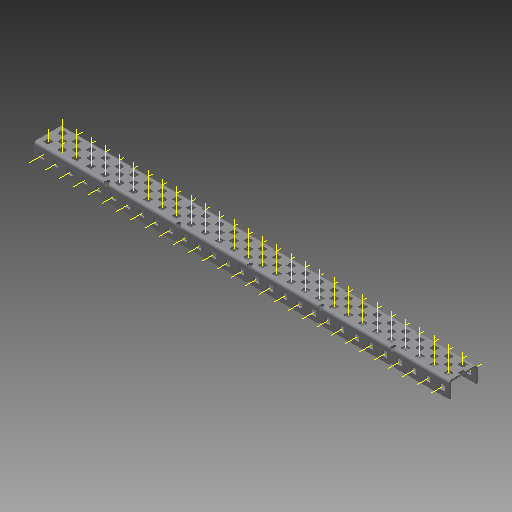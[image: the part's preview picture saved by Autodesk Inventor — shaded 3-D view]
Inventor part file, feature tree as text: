
AUTODESK INVENTOR PART (.ipt)
format: ipt  version: 2017 (Build 210142000, 142)  size: 2,218,496 bytes
history: native  units: in
note: dims shown in document units (in); Inventor stores cm internally (conversion verified against a paired STEP export)
features: other x151, pattern_linear x3, sheet_metal_op x1, extrude x1, imported_body x1, sketch x1
ambient origin geometry x8: Origin, YZ Plane, XZ Plane, XY Plane, X Axis, Y Axis, Z Axis, Center Point
bodies: Body1 (feature_tree)
feature tree (158):
  sheet_metal_op  "Fold1"
  other  "C-Channel"
  extrude  "length cut"  Depth=0.5in
  other  "top axis"
  other  "inner axis"
  other  "front axis"
  other  "back axis"
  pattern_linear  "top axes"  Spacing1=0.5in  [1 undecoded]
  pattern_linear  "inner axes"  Spacing1=0.5in  [1 undecoded]
  pattern_linear  "horiz axes"  Spacing1=-14.5in  [1 undecoded]
  other  "right plane"
  imported_body  "Base1"
  sketch  "Sketch1"  dims[d1=0.0in d4=0.5in d5=0.7874in d7=0.5in d10=0.5in d13=0.5in d14=-14.5in d15=0.0in d16=0.0in d17=0.0in d18=0.0in d19=0.0in]
  other  "Work Point1"
  other  "Work Point2"
  other  "Work Point3"
  other  "Work Point4"
  other  "Work Axis5"
  other  "Work Axis6"
  other  "Work Axis7"
  other  "Work Axis8"
  other  "Work Axis11"
  other  "Work Axis12"
  other  "Work Axis13"
  other  "Work Axis14"
  other  "Work Axis15"
  other  "Work Axis18"
  other  "Work Axis19"
  other  "Work Axis20"
  other  "Work Axis23"
  other  "Work Axis24"
  other  "Work Axis25"
  other  "Work Axis26"
  other  "Work Axis30"
  other  "Work Axis31"
  other  "Work Axis32"
  other  "Work Axis33"
  other  "left plane"
  other  "Work Axis37"
  other  "Work Axis38"
  other  "Work Axis39"
  other  "Work Axis40"
  other  "Work Axis41"
  other  "Work Axis42"
  other  "Work Axis43"
  other  "Work Axis44"
  other  "Work Axis45"
  other  "Work Axis46"
  other  "Work Axis47"
  other  "Work Axis48"
  other  "Work Axis49"
  other  "Work Axis50"
  other  "Work Axis51"
  other  "Work Axis52"
  other  "Work Axis53"
  other  "Work Axis54"
  other  "Work Axis55"
  other  "Work Axis56"
  other  "Work Axis57"
  other  "Work Axis58"
  other  "Work Axis59"
  other  "Work Axis60"
  other  "Work Axis61"
  other  "Work Axis62"
  other  "Work Axis63"
  other  "Work Axis64"
  other  "Work Axis65"
  other  "Work Axis66"
  other  "Work Axis67"
  other  "Work Axis68"
  other  "Work Axis69"
  other  "Work Axis70"
  other  "Work Axis71"
  other  "Work Axis72"
  other  "Work Axis73"
  other  "Work Axis74"
  other  "Work Axis75"
  other  "Work Axis76"
  other  "Work Axis77"
  other  "Work Axis78"
  other  "Work Axis79"
  other  "Work Axis80"
  other  "Work Axis81"
  other  "Work Axis82"
  other  "Work Axis83"
  other  "Work Axis84"
  other  "Work Axis85"
  other  "Work Axis86"
  other  "Work Axis87"
  other  "Work Axis88"
  other  "Work Axis89"
  other  "Work Axis90"
  other  "Work Axis91"
  other  "Work Axis92"
  other  "Work Axis93"
  other  "Work Axis94"
  other  "Work Axis95"
  other  "Work Axis96"
  other  "Work Axis97"
  other  "Work Axis98"
  other  "Work Axis99"
  other  "Work Axis100"
  other  "Work Axis101"
  other  "Work Axis102"
  other  "Work Axis103"
  other  "Work Axis104"
  other  "Work Axis105"
  other  "Work Axis106"
  other  "Work Axis107"
  other  "Work Axis108"
  other  "Work Axis109"
  other  "Work Axis110"
  other  "Work Axis111"
  other  "Work Axis112"
  other  "Work Axis113"
  other  "Work Axis114"
  other  "Work Axis115"
  other  "Work Axis116"
  other  "Work Axis117"
  other  "Work Axis118"
  other  "Work Axis119"
  other  "Work Axis120"
  other  "Work Axis121"
  other  "Work Axis122"
  other  "Work Axis123"
  other  "Work Axis124"
  other  "Work Axis125"
  other  "Work Axis126"
  other  "Work Axis127"
  other  "Work Axis128"
  other  "Work Axis129"
  other  "Work Axis130"
  other  "Work Axis131"
  other  "Work Axis132"
  other  "Work Axis133"
  other  "Work Axis134"
  other  "Work Axis135"
  other  "Work Axis136"
  other  "Work Axis137"
  other  "Work Axis138"
  other  "Work Axis139"
  other  "Work Axis140"
  other  "Work Axis141"
  other  "Work Axis142"
  other  "Work Axis143"
  other  "Work Axis144"
  other  "Work Axis145"
  other  "Work Axis146"
  other  "Work Axis147"
  other  "Work Axis148"
  other  "Work Axis149"
  other  "Work Axis150"
  other  "Work Axis151"
  other  "Work Axis152"
  other  "Work Axis153"
  other  "Work Axis154"
  other  "Work Axis155"
  other  "Work Axis156"
note: 3 required parameter values undecoded (feature->parameter linkage not recoverable at this tier; creation-order binding heuristic only, values carry confidence <= 0.55)
